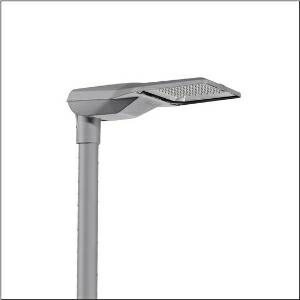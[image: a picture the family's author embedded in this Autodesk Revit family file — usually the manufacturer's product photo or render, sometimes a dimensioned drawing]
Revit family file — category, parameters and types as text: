
# Revit family: streetlight_sl_21_midi___pc-r_5xe7g43a08mb_b1b0
name_source: partatom
category: Lighting Fixtures
units: mm (PartAtom-declared; Revit-internal decimal feet)

## family parameters
Cut with Voids When Loaded = No
Host = Face
Light Source = No
Part Type = Normal
Room Calculation Point = No
Round Connector Dimension = Use Diameter
Shared = No

## types (1)
- --- (1 x LED, 19200 lm, 147 W, 4000K)
    Apparent Load = 147 VA
    CIE Flux Codes = 38 78 98 100 100
    Color Rendering = 70
    Color Temperature = 4000K
    Default Elevation = 1800 mm
    Description = Streetlight SL 21 midi, mast luminaire, primary light control with lens, of PMMA, primary optical cover: cover, of toughened safety glass, transparent, light distribution: PC-R, light emission: direct distribution, primary light characteristic: asymmetric, right, installation type: post-top, side-entry, LED, 3G 1.5mm², High Power LED, rated luminous flux: 19.200lm, luminous efficacy: 131lm/W, light colour: 740, colour temperature: 4000K, control gear: Easy, control: overheat protection, constant luminous flux control, time-dependent luminous flux control, flexible luminous flux parameterisation, mains connection: 220..240V, AC, 50/60Hz, connection cable pre-assembled, cable length: 12,5m, wiring characteristics: H07RN-F, start of lifetime: 147W, end of service life: 155W, reduction: 64W, luminaire housing, of diecast aluminium, powder-coated, Siteco® metallic grey (DB 702S), corrosivity category C5 mid according to DIN EN ISO 12944, please order mast flange separately, inclination adjustable: 0°, 5°, 10°, 15°, sealing non-destructively replaceable, multi-level sealing system, length: 644mm, width: 335mm, height: 110mm, mast flange for spigot size: 42mm (side-entry): 5XC10008XM4, 60/48mm (side-entry/post-top): 5XC10108XM2, 76/60mm (side-entry/post-top): 5XC10108XM1, mounting height: 4..8m, protection rating (complete): IP66, insulation class (complete): insulation class II (safety insulation), certification: CE, ENEC, ENEC+, VDE, impact resistance: IK10, permissible operating ambient temperature for outdoor applications: -40..+50°C, standard-compliant lighting for roads and squares, packaging unit: 1 piece

Light Distribution: PC-R
    Height = 111 mm
    Lamp = 1 x LED
    Lamp Light Flux = 19200 lm
    Lamp Power = 147 W
    Lamp count = 1
    Length = 644 mm
    Luminous efficacy = 131 lm/W
    Manufacturer = Siteco
    ModVariant = No
    Model = 5XE7G43A08MB
    Number of Poles = 1
    OnlyDefault = Yes
    Power Factor = 1
    Product Name = Streetlight SL 21 midi | PC-R
    Product group = mast luminaire | pylon top
    ProductGroupID = 6100
    Protection Class = Protection class II
    Protection Degree = IP 66
    RLX_Detail_Level = 1
    RLX_Emergency_Light_Flux = 0 lm
    RLX_Emergency_Type = 0
    RLX_Emergency_Type_DB = No
    RlxData = <blob elided: 29261 chars, md5=7e8ccd33>
    Socket = socket
    Standby Power = 0 W
    System Light Flux = 19200 lm
    System Power = 147 W
    Type Comments = factory setting: luminous flux: 100 % | Output Level: 100 % | 750 mA
    Type Image = l_1004298.jpg
    URL = http://relux.com
    VarID = @adj_064122
    Voltage = 0 V
    Weight = 0.00 kg
    Width = 336 mm

## geometry (parser evidence)
native form markers: Blend x4, Sweep x10
no freeform markers — native parametric forms only
